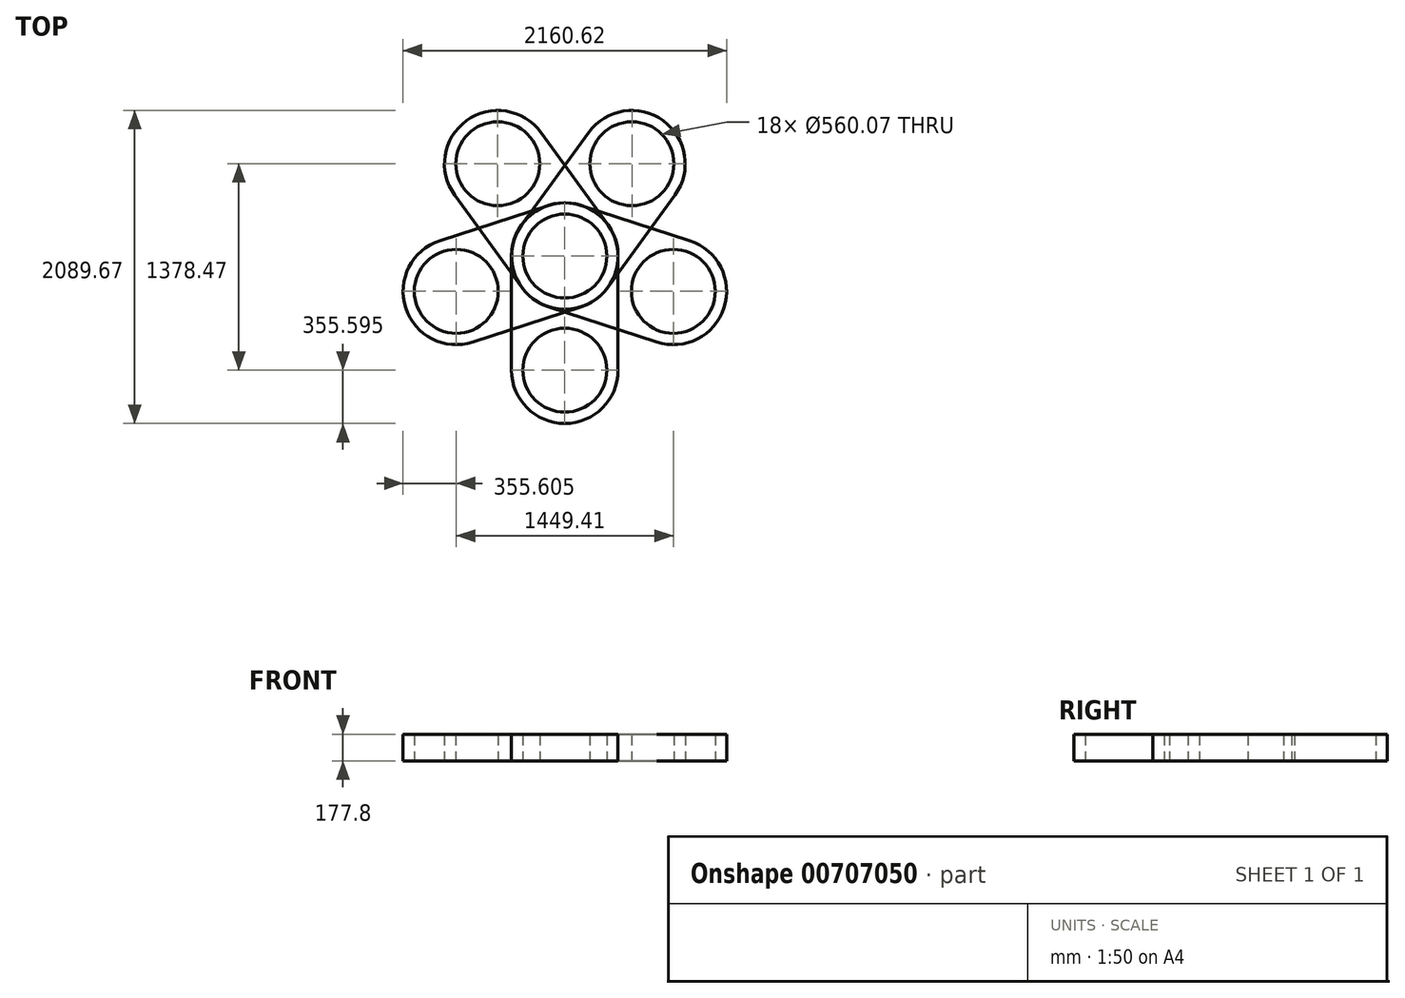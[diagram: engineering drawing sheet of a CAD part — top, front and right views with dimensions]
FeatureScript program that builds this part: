
annotation { "Feature Type Name" : "Feature", "Feature Type Description" : "" }
export const myFeature = defineFeature(function(context is Context, id is Id, definition is map)
    precondition{}
    {
        {
            var Q0;
            Q0=qCreatedBy(makeId("Top.planeOp"),FACE);
            var sketch = newSketch(context, id + "F0", { "sketchPlane" : qUnion([Q0])});
            skLineSegment(sketch, "E0.bottom", {"start": v(0, 248.49) * mm, "end": v(711.2, 248.49) * mm});
            skLineSegment(sketch, "E0.top", {"start": v(0, -513.51) * mm, "end": v(711.2, -513.51) * mm});
            skLineSegment(sketch, "E0.left", {"start": v(0, 248.49) * mm, "end": v(0, -513.51) * mm});
            skLineSegment(sketch, "E0.right", {"start": v(711.2, 248.49) * mm, "end": v(711.2, -513.51) * mm});
            skCircle(sketch, "E1", {"center": v(355.6, -513.51) * mm, "radius": 355.6 * mm});
            skCircle(sketch, "E2", {"center": v(355.6, -513.51) * mm, "radius": 280.04 * mm});
            skCircle(sketch, "E3", {"center": v(355.6, 248.49) * mm, "radius": 355.6 * mm});
            skCircle(sketch, "E4", {"center": v(355.6, 248.49) * mm, "radius": 280.04 * mm});
            skSolve(sketch);
        }
        {
            var Q0;
            {var subQ1=sQuery(id+"F0.wireOp",EDGE,"E0.top");var subQ3=sQuery(id+"F0.wireOp",EDGE,"E2");var subQ4=makeQuery(id+"F0.imprint","INTERSECT",VERTEX,{"disambiguationData":[OD(0.0)],"derivedFrom":[subQ1,subQ3]});Q0=makeQuery(id+"F0.imprint","IMPRINT",FACE,{"disambiguationData":[TD([[makeQuery(id+"F0.imprint","IMPRINT",EDGE,{"disambiguationData":[TD([[subQ4,-1.0]])],"derivedFrom":subQ3}),-1.0]])]});}
            var Q1;
            {var subQ1=sQuery(id+"F0.wireOp",EDGE,"E0.top");var subQ3=sQuery(id+"F0.wireOp",EDGE,"E2");var subQ4=makeQuery(id+"F0.imprint","INTERSECT",VERTEX,{"disambiguationData":[OD(0.0)],"derivedFrom":[subQ1,subQ3]});Q1=makeQuery(id+"F0.imprint","IMPRINT",FACE,{"disambiguationData":[TD([[makeQuery(id+"F0.imprint","IMPRINT",EDGE,{"disambiguationData":[TD([[subQ4,1.0]])],"derivedFrom":subQ3}),-1.0]])]});}
            var Q2;
            {var subQ0=sQuery(id+"F0.wireOp",EDGE,"E0.left");Q2=makeQuery(id+"F0.imprint","IMPRINT",FACE,{"disambiguationData":[TD([[makeQuery(id+"F0.imprint","IMPRINT",EDGE,{"derivedFrom":subQ0}),1.0]])]});}
            var Q3;
            {var subQ1=sQuery(id+"F0.wireOp",EDGE,"E0.bottom");var subQ3=sQuery(id+"F0.wireOp",EDGE,"E4");var subQ4=makeQuery(id+"F0.imprint","INTERSECT",VERTEX,{"disambiguationData":[OD(0.0)],"derivedFrom":[subQ1,subQ3]});Q3=makeQuery(id+"F0.imprint","IMPRINT",FACE,{"disambiguationData":[TD([[makeQuery(id+"F0.imprint","IMPRINT",EDGE,{"disambiguationData":[TD([[subQ4,-1.0]])],"derivedFrom":subQ3}),-1.0]])]});}
            var Q4;
            {var subQ1=sQuery(id+"F0.wireOp",EDGE,"E0.bottom");var subQ3=sQuery(id+"F0.wireOp",EDGE,"E4");var subQ4=makeQuery(id+"F0.imprint","INTERSECT",VERTEX,{"disambiguationData":[OD(0.0)],"derivedFrom":[subQ1,subQ3]});Q4=makeQuery(id+"F0.imprint","IMPRINT",FACE,{"disambiguationData":[TD([[makeQuery(id+"F0.imprint","IMPRINT",EDGE,{"disambiguationData":[TD([[subQ4,1.0]])],"derivedFrom":subQ3}),-1.0]])]});}
            extrude(context, id + "F1", {"entities" : qUnion([Q0, Q1, Q2, Q3, Q4]), "depth" : 177.8 * mm, "offsetDistance" : 25.4 * mm});
        }
        {
            var Q0;
            Q0=makeQuery(id+"F1.opExtrude","SWEPT_BODY",BODY,{"disambiguationData":[OSD([sQuery(id+"F0.wireOp",EDGE,"E0.left"),sQuery(id+"F0.wireOp",EDGE,"E0.right"),sQuery(id+"F0.wireOp",EDGE,"E1"),sQuery(id+"F0.wireOp",EDGE,"E2"),sQuery(id+"F0.wireOp",EDGE,"E3"),sQuery(id+"F0.wireOp",EDGE,"E4")])]});
            var Q1;
            Q1=makeQuery(id+"F1.opExtrude","CAP_EDGE",EDGE,{"disambiguationData":[OSD([sQuery(id+"F0.wireOp",EDGE,"E4")])],"isStart":false});
            circularPattern(context, id + "F2", {"entities" : qUnion([Q0]), "axis" : qUnion([Q1]), "angle" : 360 * degree, "instanceCount" : 5, "equalSpace" : true, "isCentered" : true});
        }
    });
